FCSTD DOCUMENT  (FreeCAD 0.17R8349 (Git))
Label: ShaftSealRing_DIN3760_FormA
License: All rights reserved
LicenseURL: http://en.wikipedia.org/wiki/All_rights_reserved
objects: Sketcher::SketchObject×1
note: 1 computed .brp shape members not serialized (recipe doc carries the construction recipe); baked Part::Feature solids carry a one-line shape summary decoded from their .brp

FEATURE [Sketcher::SketchObject] sketch
  sketch-geometry (33):
    g0: LineSegment StartX=0 StartY=7.7 StartZ=0 EndX=0.3 EndY=8 EndZ=0
    g1: LineSegment StartX=0.3 StartY=8 StartZ=0 EndX=6.7 EndY=8 EndZ=0
    g2: LineSegment StartX=6.7 StartY=8 StartZ=0 EndX=7 EndY=7.7 EndZ=0
    g3: LineSegment StartX=7 StartY=7.7 StartZ=0 EndX=7 EndY=1.1359 EndZ=0
    g4: LineSegment StartX=6.7 StartY=0.835898 StartZ=0 EndX=2.6 EndY=0.835898 EndZ=0
    g5: LineSegment StartX=2.3 StartY=0.535898 StartZ=0 EndX=2.3 EndY=0.267949 EndZ=0
    g6: LineSegment StartX=2.3 StartY=0.267949 StartZ=0 EndX=1.3 EndY=0 EndZ=0
    g7: LineSegment StartX=1.3 StartY=0 StartZ=0 EndX=0.3 EndY=1 EndZ=0
    g8: LineSegment StartX=0.3 StartY=1 StartZ=0 EndX=0.3 EndY=1.5359 EndZ=0
    g9: LineSegment StartX=0.6 StartY=1.8359 StartZ=0 EndX=4.7 EndY=1.8359 EndZ=0
    g10: LineSegment StartX=5 StartY=2.1359 StartZ=0 EndX=5 EndY=5.7 EndZ=0
    g11: LineSegment StartX=4.7 StartY=6 StartZ=0 EndX=0.3 EndY=6 EndZ=0
    g12: LineSegment StartX=0.3 StartY=6 StartZ=0 EndX=0 EndY=6.3 EndZ=0
    g13: LineSegment StartX=0 StartY=6.3 StartZ=0 EndX=0 EndY=7.7 EndZ=0
    g14: ArcOfCircle CenterX=4.7 CenterY=5.7 CenterZ=0 NormalX=0 NormalY=0 NormalZ=1 Radius=0.3 StartAngle=0 EndAngle=1.5708
    g15: ArcOfCircle CenterX=6.7 CenterY=1.1359 CenterZ=0 NormalX=0 NormalY=0 NormalZ=1 Radius=0.3 StartAngle=4.71239 EndAngle=6.28319
    g16: ArcOfCircle CenterX=2.6 CenterY=0.535898 CenterZ=0 NormalX=0 NormalY=0 NormalZ=1 Radius=0.3 StartAngle=1.5708 EndAngle=3.14159
    g17: ArcOfCircle CenterX=4.7 CenterY=2.1359 CenterZ=0 NormalX=0 NormalY=0 NormalZ=1 Radius=0.3 StartAngle=4.71239 EndAngle=6.28319
    g18: ArcOfCircle CenterX=0.6 CenterY=1.5359 CenterZ=0 NormalX=0 NormalY=0 NormalZ=1 Radius=0.3 StartAngle=1.5708 EndAngle=3.14159
    g19: LineSegment [constr] StartX=0.3 StartY=8 StartZ=0 EndX=0 EndY=8 EndZ=0
    g20: LineSegment [constr] StartX=7 StartY=7.7 StartZ=0 EndX=7 EndY=8 EndZ=0
    g21: LineSegment [constr] StartX=6.7 StartY=8 StartZ=0 EndX=7 EndY=8 EndZ=0
    g22: LineSegment [constr] StartX=4.7 StartY=6 StartZ=0 EndX=4.7 EndY=8 EndZ=0
    g23: LineSegment [constr] StartX=5 StartY=5.7 StartZ=0 EndX=7 EndY=5.7 EndZ=0
    g24: LineSegment [constr] StartX=4.7 StartY=1.8359 StartZ=0 EndX=4.7 EndY=0.835898 EndZ=0
    g25: LineSegment [constr] StartX=4.7 StartY=5.7 StartZ=0 EndX=4.7 EndY=6 EndZ=0
    g26: LineSegment [constr] StartX=0.3 StartY=8 StartZ=0 EndX=0.3 EndY=1.5359 EndZ=0
    g27: LineSegment [constr] StartX=0.3 StartY=1 StartZ=0 EndX=2.3 EndY=1 EndZ=0
    g28: LineSegment [constr] StartX=1.3 StartY=0 StartZ=0 EndX=1.3 EndY=1 EndZ=0
    g29: LineSegment [constr] StartX=2.3 StartY=0.267949 StartZ=0 EndX=2.3 EndY=0 EndZ=0
    g30: LineSegment [constr] StartX=4.7 StartY=6 StartZ=0 EndX=4.7 EndY=4 EndZ=0
    g31: LineSegment [constr] StartX=4.7 StartY=4 StartZ=0 EndX=4.7 EndY=2 EndZ=0
    g32: LineSegment [constr] StartX=4.7 StartY=2 StartZ=0 EndX=4.7 EndY=0 EndZ=0
  constraints (91):
    c: PointOnObject(g0,g-2)
    c: Coincident(g0,g1)
    c: Horizontal(g1)
    c: Coincident(g1,g2)
    c: Coincident(g2,g3)
    c: Vertical(g3)
    c: Horizontal(g4)
    c: Coincident(g5,g6)
    c: PointOnObject(g6,g-1)
    c: Coincident(g6,g7)
    c: Coincident(g7,g8)
    c: Horizontal(g9)
    c: Horizontal(g11)
    c: Coincident(g11,g12)
    c: PointOnObject(g12,g-2)
    c: Coincident(g12,g13)
    c: Coincident(g13,g0)
    c: Vertical(g10)
    c: Tangent(g11,g14) = -1.5708
    c: Tangent(g10,g14) = -1.5708
    c: Tangent(g3,g15) = 1.5708
    c: Tangent(g4,g15) = 1.5708
    c: Tangent(g5,g16) = -1.5708
    c: Tangent(g4,g16) = -1.5708
    c: Tangent(g9,g17) = -1.5708
    c: Tangent(g10,g17) = -1.5708
    c: Tangent(g8,g18) = 1.5708
    c: Tangent(g9,g18) = 1.5708
    c: Vertical(g8)
    c: Coincident(g19,g0)
    c: PointOnObject(g19,g-2)
    c: Horizontal(g19)
    c: Coincident(g20,g2)
    c: Vertical(g20)
    c: Coincident(g21,g1)
    c: Coincident(g21,g20)
    c: Horizontal(g21)
    c: Equal(g21,g19)
    c: DistanceX(g19,g0) = 0.3  'c'
    c: DistanceX(g19,g20) = 7  'b'
    c: Angle(g19,g0) = 0.785398
    c: Angle(g2,g21) = 0.785398
    c: Vertical(g5)
    c: Angle(g7,g8) = 2.35619
    c: Angle(g6,g7) = 2.0944
    c: DistanceY(g-1,g19) = 8  'H'
    c: Angle(g12,g13) = 2.35619
    c: Equal(g0,g12)
    c: Coincident(g22,g11)
    c: PointOnObject(g22,g1)
    c: Vertical(g22)
    c: Coincident(g23,g10)
    c: PointOnObject(g23,g3)
    c: Horizontal(g23)
    c: Equal(g23,g22)
    c: Equal(g14,g17)
    c: Equal(g14,g15)
    c: Equal(g16,g14)
    c: Equal(g18,g14)
    c: Coincident(g24,g9)
    c: PointOnObject(g24,g4)
    c: Vertical(g24)
    c: Coincident(g25,g14)
    c: Coincident(g25,g11)
    c: Equal(g25,g19)
    c: Coincident(g26,g0)
    c: Coincident(g26,g8)
    c: Vertical(g26)
    c: Coincident(g27,g7)
    c: PointOnObject(g27,g5)
    c: Horizontal(g27)
    c: Coincident(g28,g6)
    c: PointOnObject(g28,g27)
    c: Vertical(g28)
    c: Symmetric(g27,g7,g28)
    c: Equal(g27,g22)
    c: Coincident(g29,g5)
    c: PointOnObject(g29,g-1)
    c: Vertical(g29)
    c: Equal(g29,g5)
    c: Equal(g28,g24)
    c: Coincident(g30,g11)
    c: Vertical(g30)
    c: Coincident(g31,g30)
    c: Vertical(g31)
    c: Coincident(g32,g31)
    c: PointOnObject(g32,g-1)
    c: Vertical(g32)
    c: Equal(g22,g31)
    c: Equal(g30,g22)
    c: Equal(g22,g32)
